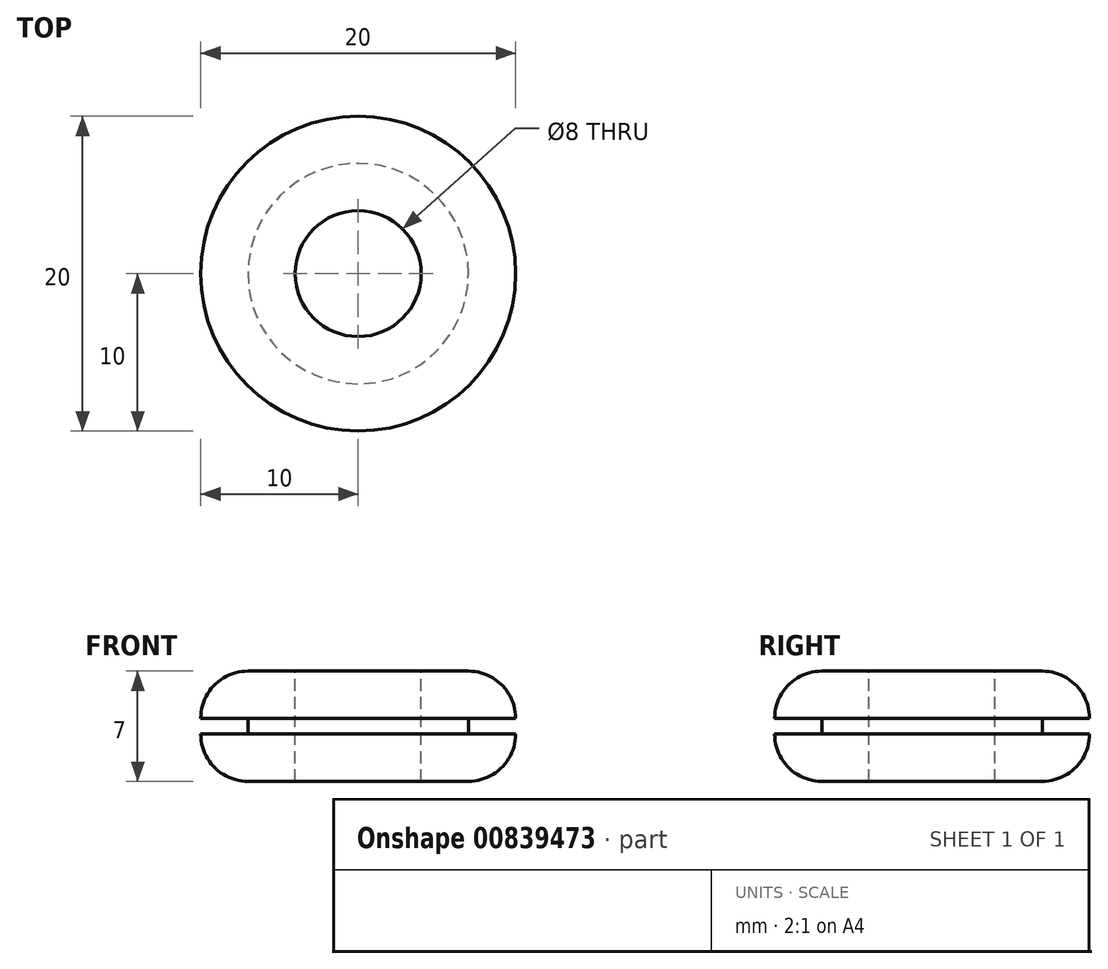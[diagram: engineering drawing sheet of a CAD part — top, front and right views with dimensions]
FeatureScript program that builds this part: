
annotation { "Feature Type Name" : "Feature", "Feature Type Description" : "" }
export const myFeature = defineFeature(function(context is Context, id is Id, definition is map)
    precondition{}
    {
        {
            var Q0;
            Q0=qCreatedBy(makeId("Front.planeOp"),FACE);
            var sketch = newSketch(context, id + "F0", { "sketchPlane" : qUnion([Q0])});
            skLineSegment(sketch, "E0.bottom", {"start": v(4, -3.5) * mm, "end": v(7, -3.5) * mm});
            skLineSegment(sketch, "E0.top", {"start": v(4, 3.5) * mm, "end": v(7, 3.5) * mm});
            skLineSegment(sketch, "E0.left", {"start": v(4, -3.5) * mm, "end": v(4, 3.5) * mm});
            skPoint(sketch, "E1.visualSharp", {"position": v(10, 3.5) * mm});
            skArc(sketch, "E1.filletArc", {"start": v(10, 0.5) * mm, "mid": v(9.12, 2.62) * mm, "end": v(7, 3.5) * mm});
            skPoint(sketch, "E2.visualSharp", {"position": v(10, -3.5) * mm});
            skArc(sketch, "E2.filletArc", {"start": v(7, -3.5) * mm, "mid": v(9.12, -2.62) * mm, "end": v(10, -0.5) * mm});
            skLineSegment(sketch, "E3.bottom", {"start": v(7, 0.5) * mm, "end": v(10, 0.5) * mm});
            skLineSegment(sketch, "E3.top", {"start": v(7, -0.5) * mm, "end": v(10, -0.5) * mm});
            skLineSegment(sketch, "E3.left", {"start": v(7, 0.5) * mm, "end": v(7, -0.5) * mm});
            skLineSegment(sketch, "E4", {"start": v(0, 0) * mm, "end": v(10, 0) * mm, "construction": true});
            skLineSegment(sketch, "E5", {"start": v(0, 21.18) * mm, "end": v(0, -22.05) * mm, "construction": true});
            skSolve(sketch);
        }
        {
            var Q0;
            Q0=makeQuery(id+"F0.imprint","IMPRINT",FACE,{"disambiguationData":[TD([[makeQuery(id+"F0.imprint","IMPRINT",EDGE,{"derivedFrom":sQuery(id+"F0.wireOp",EDGE,"E0.bottom")}),1.0]])]});
            var Q1;
            Q1=sQuery(id+"F0.wireOp",EDGE,"E5");
            revolve(context, id + "F1", {"surfaceOperationType" : NewSurfaceOperationType.NEW, "entities" : qUnion([Q0]), "axis" : qUnion([Q1]), "revolveType" : RevolveType.FULL});
        }
    });
